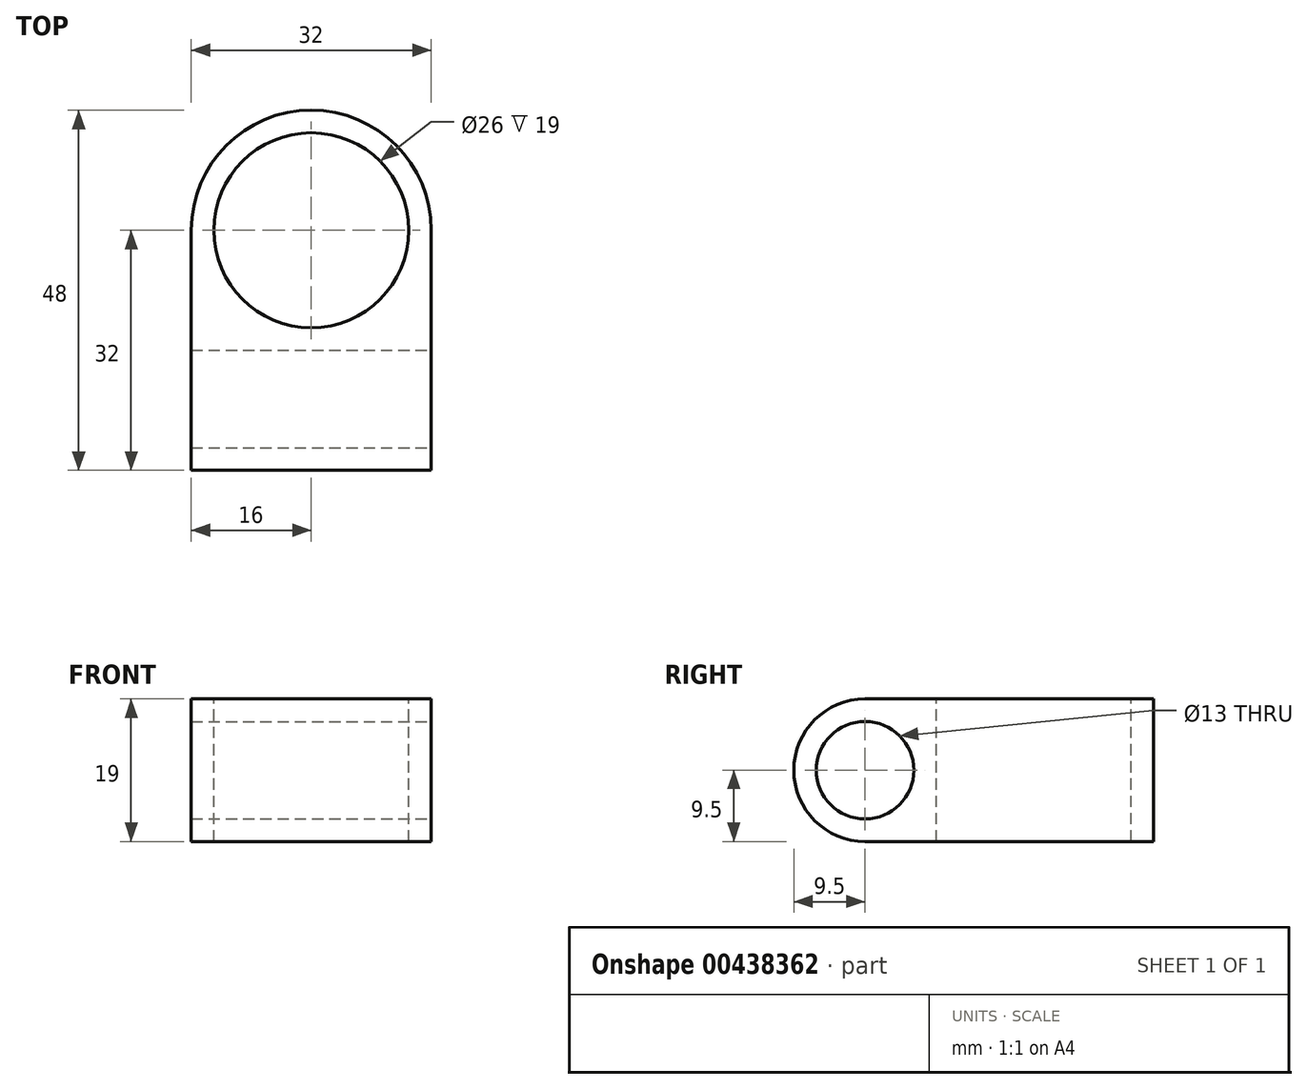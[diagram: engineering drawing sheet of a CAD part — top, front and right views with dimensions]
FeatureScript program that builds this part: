
annotation { "Feature Type Name" : "Feature", "Feature Type Description" : "" }
export const myFeature = defineFeature(function(context is Context, id is Id, definition is map)
    precondition{}
    {
        {
            var Q0;
            Q0=qCreatedBy(makeId("Top.planeOp"),FACE);
            var sketch = newSketch(context, id + "F0", { "sketchPlane" : qUnion([Q0])});
            skCircle(sketch, "E0.0", {"center": v(0, 0) * mm, "radius": 16 * mm});
            skSolve(sketch);
        }
        {
            var Q0;
            Q0 = qSketchRegion(id + "F0", true);
            extrude(context, id + "F1", {"entities" : qUnion([Q0]), "depth" : 19 * mm});
        }
        {
            var Q0;
            Q0=qCreatedBy(makeId("Right.planeOp"),FACE);
            var sketch = newSketch(context, id + "F2", { "sketchPlane" : qUnion([Q0])});
            skArc(sketch, "E1.0", {"start": v(-22.5, 19) * mm, "mid": v(-32, 9.5) * mm, "end": v(-22.5, 0) * mm});
            skLineSegment(sketch, "E2", {"start": v(0, 0) * mm, "end": v(0, 19) * mm});
            skLineSegment(sketch, "E3", {"start": v(0, 19) * mm, "end": v(-22.5, 19) * mm});
            skLineSegment(sketch, "E4", {"start": v(0, 0) * mm, "end": v(-22.5, 0) * mm});
            skSolve(sketch);
        }
        {
            var Q0;
            Q0 = qSketchRegion(id + "F2", true);
            extrude(context, id + "F3", {"entities" : qUnion([Q0]), "operationType" : NewBodyOperationType.ADD, "endBound" : BoundingType.SYMMETRIC, "depth" : 32 * mm});
        }
        {
            var Q0;
            Q0=makeQuery(id+"F3.boolean.opBoolean","MERGE",FACE,{"derivedFrom":[makeQuery(id+"F1.opExtrude","CAP_FACE",FACE,{"disambiguationData":[OSD([sQuery(id+"F0.wireOp",EDGE,"E0.0")])],"isStart":false}),makeQuery(id+"F3.opExtrude","SWEPT_FACE",FACE,{"disambiguationData":[OSD([sQuery(id+"F2.wireOp",EDGE,"E3")])]})]});
            var sketch = newSketch(context, id + "F4", { "sketchPlane" : qUnion([Q0])});
            skCircle(sketch, "E5", {"center": v(0, 0) * mm, "radius": 13 * mm});
            skSolve(sketch);
        }
        {
            var Q0;
            Q0 = qSketchRegion(id + "F4", true);
            extrude(context, id + "F5", {"entities" : qUnion([Q0]), "operationType" : NewBodyOperationType.REMOVE, "oppositeDirection" : true, "depth" : 25 * mm});
        }
        {
            var Q0;
            Q0=makeQuery(id+"F3.opExtrude","CAP_FACE",FACE,{"disambiguationData":[OSD([sQuery(id+"F2.wireOp",EDGE,"E1.0"),sQuery(id+"F2.wireOp",EDGE,"E2"),sQuery(id+"F2.wireOp",EDGE,"E3"),sQuery(id+"F2.wireOp",EDGE,"E4")])],"isStart":false});
            var sketch = newSketch(context, id + "F6", { "sketchPlane" : qUnion([Q0])});
            skCircle(sketch, "E6", {"center": v(-22.5, 9.5) * mm, "radius": 6.5 * mm});
            skSolve(sketch);
        }
        {
            var Q0;
            Q0 = qSketchRegion(id + "F6", true);
            extrude(context, id + "F7", {"entities" : qUnion([Q0]), "operationType" : NewBodyOperationType.REMOVE, "endBound" : BoundingType.THROUGH_ALL, "oppositeDirection" : true, "depth" : 25 * mm});
        }
    });
